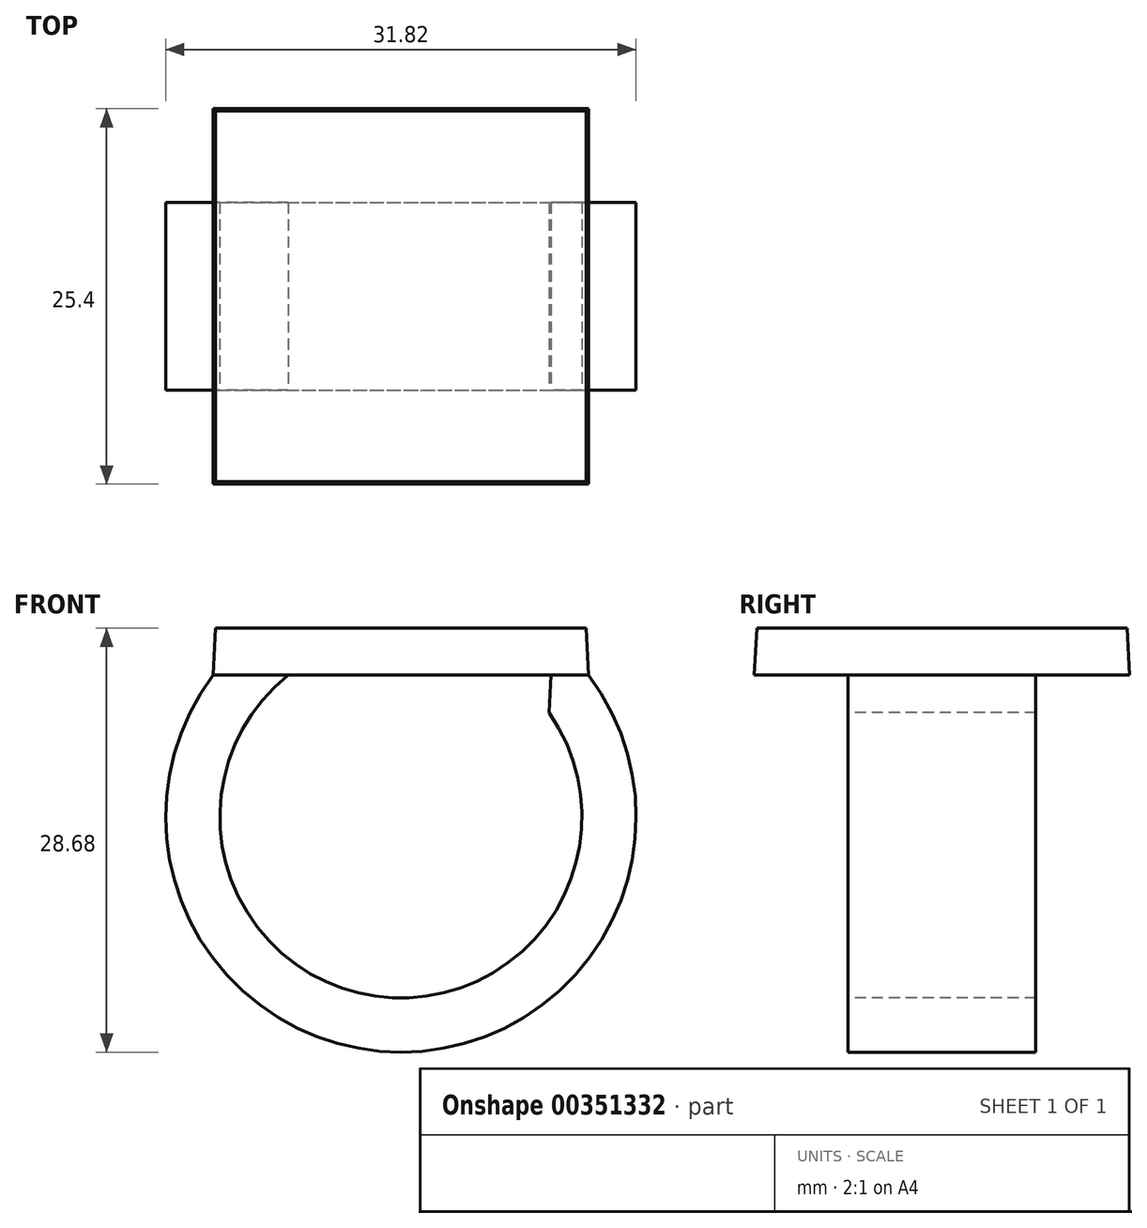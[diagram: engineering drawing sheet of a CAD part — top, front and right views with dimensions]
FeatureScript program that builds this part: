
annotation { "Feature Type Name" : "Feature", "Feature Type Description" : "" }
export const myFeature = defineFeature(function(context is Context, id is Id, definition is map)
    precondition{}
    {
        {
            var Q0;
            Q0=qCreatedBy(makeId("Top.planeOp"),FACE);
            var sketch = newSketch(context, id + "F0", { "sketchPlane" : qUnion([Q0])});
            skLineSegment(sketch, "E0.bottom", {"start": v(-12.7, 12.7) * mm, "end": v(12.7, 12.7) * mm});
            skLineSegment(sketch, "E0.top", {"start": v(-12.7, -12.7) * mm, "end": v(12.7, -12.7) * mm});
            skLineSegment(sketch, "E0.left", {"start": v(-12.7, 12.7) * mm, "end": v(-12.7, -12.7) * mm});
            skLineSegment(sketch, "E0.right", {"start": v(12.7, 12.7) * mm, "end": v(12.7, -12.7) * mm});
            skPoint(sketch, "E0.middle", {"position": v(0, 0) * mm});
            skSolve(sketch);
        }
        {
            var Q0;
            Q0 = qSketchRegion(id + "F0", true);
            extrude(context, id + "F1", {"entities" : qUnion([Q0]), "depth" : 3.17 * mm, "hasDraft" : true, "draftAngle" : 3 * degree, "draftPullDirection" : true});
        }
        {
            var Q0;
            Q0=qCreatedBy(makeId("Front.planeOp"),FACE);
            var sketch = newSketch(context, id + "F2", { "sketchPlane" : qUnion([Q0])});
            skArc(sketch, "E1", {"start": v(-10.16, 0) * mm, "mid": v(0, -23.56) * mm, "end": v(10.16, 0) * mm});
            skSolve(sketch);
        }
        {
            var Q0;
            Q0=makeQuery(id+"F1.opExtrude","CAP_FACE",FACE,{"disambiguationData":[OSD([sQuery(id+"F0.wireOp",EDGE,"E0.bottom"),sQuery(id+"F0.wireOp",EDGE,"E0.top"),sQuery(id+"F0.wireOp",EDGE,"E0.left"),sQuery(id+"F0.wireOp",EDGE,"E0.right")])],"isStart":true});
            var sketch = newSketch(context, id + "F3", { "sketchPlane" : qUnion([Q0])});
            skLineSegment(sketch, "E2.bottom", {"start": v(-7.62, -6.35) * mm, "end": v(-12.7, -6.35) * mm});
            skLineSegment(sketch, "E2.top", {"start": v(-7.62, 6.35) * mm, "end": v(-12.7, 6.35) * mm});
            skLineSegment(sketch, "E2.left", {"start": v(-7.62, -6.35) * mm, "end": v(-7.62, 6.35) * mm});
            skLineSegment(sketch, "E2.right", {"start": v(-12.7, -6.35) * mm, "end": v(-12.7, 6.35) * mm});
            skPoint(sketch, "E2.middle", {"position": v(-10.16, 0) * mm});
            skSolve(sketch);
        }
        {
            var Q0;
            Q0 = qSketchRegion(id + "F3", true);
            var Q1;
            Q1 = qConstructionFilter(qBodyType(qCreatedBy(id + "F2" ,EDGE), BodyType.WIRE), ConstructionObject.NO);
            sweep(context, id + "F4", {"operationType" : NewBodyOperationType.ADD, "profiles" : qUnion([Q0]), "path" : qUnion([Q1])});
        }
    });
